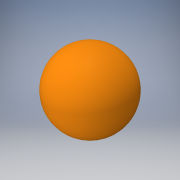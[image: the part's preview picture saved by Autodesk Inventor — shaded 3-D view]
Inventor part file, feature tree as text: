
AUTODESK INVENTOR PART (.ipt)
format: ipt  version: 2016 (Build 200138000, 138)  size: 147,456 bytes
history: native  units: in
note: dims shown in document units (in); Inventor stores cm internally (conversion verified against a paired STEP export)
features: revolve x1, sketch x1
ambient origin geometry x8: Origin, YZ Plane, XZ Plane, XY Plane, X Axis, Y Axis, Z Axis, Center Point
bodies: Solid1 (feature_tree)
feature tree (2):
  revolve  "Revolution1"  [1 undecoded]
  sketch  "Sketch1"  dims[d0=9.3937in d1=9.2362in d2=90.0deg]
note: 1 required parameter value undecoded (feature->parameter linkage not recoverable at this tier; creation-order binding heuristic only, values carry confidence <= 0.55)
